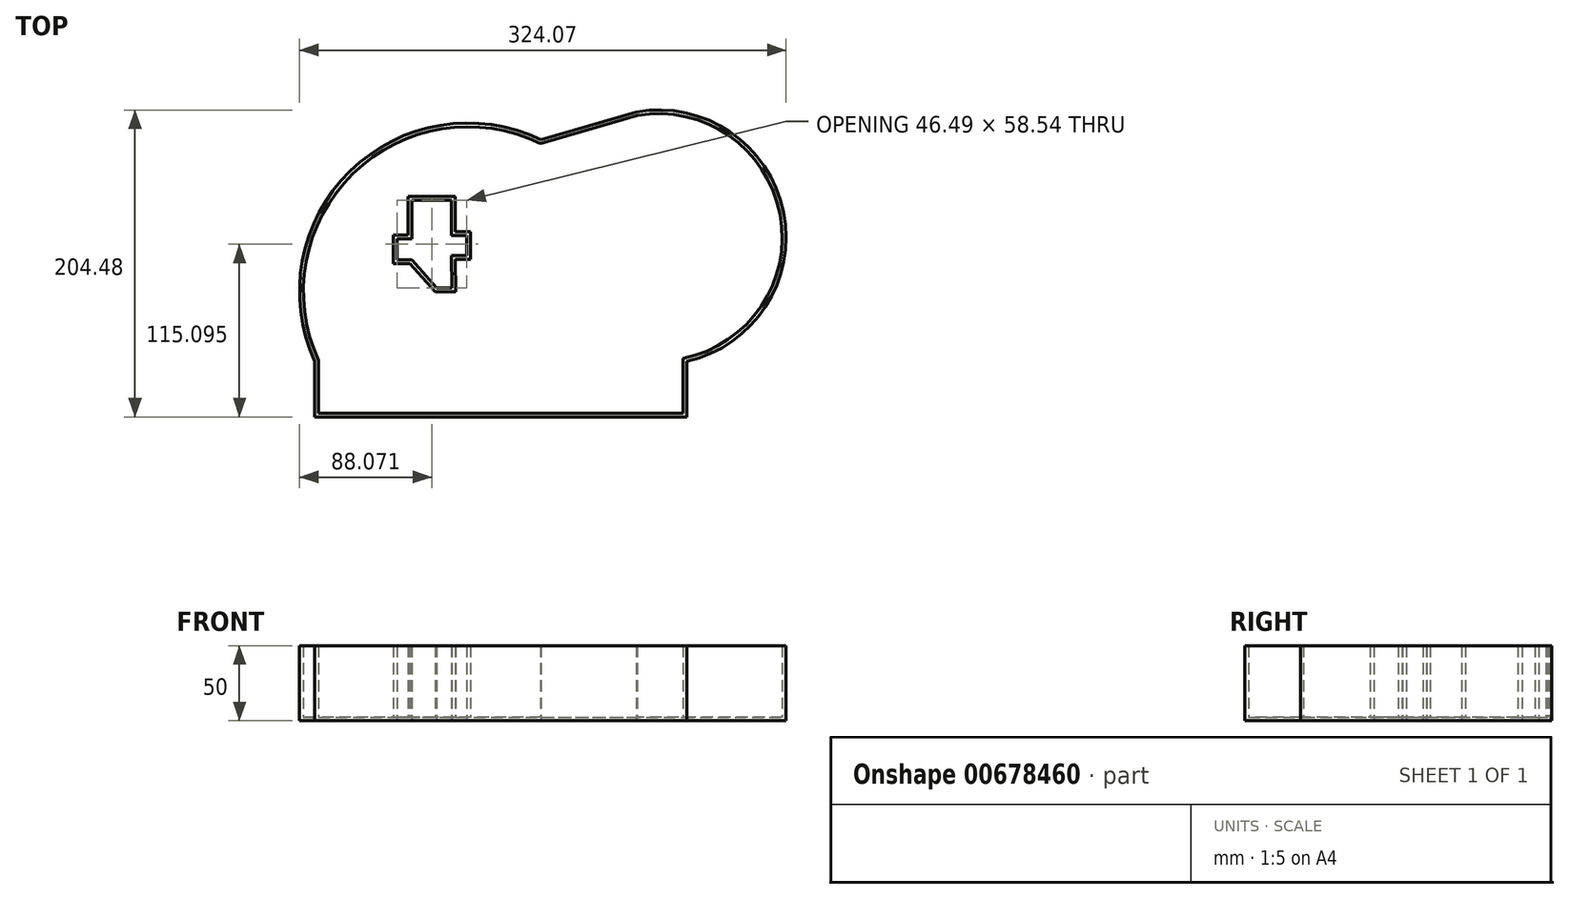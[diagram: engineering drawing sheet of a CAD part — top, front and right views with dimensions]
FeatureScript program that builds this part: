
annotation { "Feature Type Name" : "Feature", "Feature Type Description" : "" }
export const myFeature = defineFeature(function(context is Context, id is Id, definition is map)
    precondition{}
    {
        {
            var Q0;
            Q0=qCreatedBy(makeId("Top.planeOp"),FACE);
            var sketch = newSketch(context, id + "F0", { "sketchPlane" : qUnion([Q0])});
            skLineSegment(sketch, "E0", {"start": v(-101.67, -66.95) * mm, "end": v(-101.67, -103.92) * mm});
            skLineSegment(sketch, "E1", {"start": v(-101.67, -103.92) * mm, "end": v(146.19, -103.92) * mm});
            skLineSegment(sketch, "E2", {"start": v(146.19, -103.92) * mm, "end": v(146.19, -66.95) * mm});
            skArc(sketch, "E3", {"start": v(49.06, 80.77) * mm, "mid": v(-78.15, 59.81) * mm, "end": v(-101.67, -66.95) * mm});
            skLineSegment(sketch, "E4", {"start": v(49.06, 80.77) * mm, "end": v(112.57, 99.25) * mm});
            skArc(sketch, "E5", {"start": v(146.19, -66.95) * mm, "mid": v(210.57, 32.57) * mm, "end": v(112.57, 99.25) * mm});
            skLineSegment(sketch, "E6", {"start": v(-37, 0.67) * mm, "end": v(-47, 0.67) * mm});
            skLineSegment(sketch, "E7", {"start": v(-47, 0.67) * mm, "end": v(-47, 14.81) * mm});
            skLineSegment(sketch, "E8", {"start": v(-47, 14.81) * mm, "end": v(-37, 14.81) * mm});
            skLineSegment(sketch, "E9", {"start": v(-37, 14.81) * mm, "end": v(-37, 40.45) * mm});
            skLineSegment(sketch, "E10", {"start": v(-37, 40.45) * mm, "end": v(-10.77, 40.45) * mm});
            skLineSegment(sketch, "E11", {"start": v(-10.77, 40.45) * mm, "end": v(-10.7, 16.93) * mm});
            skLineSegment(sketch, "E12", {"start": v(-10.7, 16.93) * mm, "end": v(-0.54, 16.95) * mm});
            skLineSegment(sketch, "E13", {"start": v(-0.54, 16.95) * mm, "end": v(-0.5, 3.68) * mm});
            skLineSegment(sketch, "E14", {"start": v(-0.5, 3.68) * mm, "end": v(-10.5, 3.65) * mm});
            skLineSegment(sketch, "E15", {"start": v(-10.5, 3.65) * mm, "end": v(-10.4, -18.04) * mm});
            skLineSegment(sketch, "E16", {"start": v(-10.4, -18.04) * mm, "end": v(-20.4, -18.1) * mm});
            skLineSegment(sketch, "E17", {"start": v(-20.4, -18.1) * mm, "end": v(-37, 0.67) * mm});
            skSolve(sketch);
        }
        {
            var Q0;
            Q0=makeQuery(id+"F0.imprint","IMPRINT",FACE,{"disambiguationData":[TD([[makeQuery(id+"F0.imprint","IMPRINT",EDGE,{"derivedFrom":sQuery(id+"F0.wireOp",EDGE,"E0")}),1.0]])]});
            extrude(context, id + "F1", {"entities" : qUnion([Q0]), "depth" : 50 * mm, "offsetDistance" : 25 * mm});
        }
        {
            var Q0;
            Q0=makeQuery(id+"F1.opExtrude","CAP_FACE",FACE,{"disambiguationData":[OSD([sQuery(id+"F0.wireOp",EDGE,"E0"),sQuery(id+"F0.wireOp",EDGE,"E1"),sQuery(id+"F0.wireOp",EDGE,"E2"),sQuery(id+"F0.wireOp",EDGE,"E3"),sQuery(id+"F0.wireOp",EDGE,"E4"),sQuery(id+"F0.wireOp",EDGE,"E5"),sQuery(id+"F0.wireOp",EDGE,"E6"),sQuery(id+"F0.wireOp",EDGE,"E7"),sQuery(id+"F0.wireOp",EDGE,"E8"),sQuery(id+"F0.wireOp",EDGE,"E9"),sQuery(id+"F0.wireOp",EDGE,"E10"),sQuery(id+"F0.wireOp",EDGE,"E11"),sQuery(id+"F0.wireOp",EDGE,"E12"),sQuery(id+"F0.wireOp",EDGE,"E13"),sQuery(id+"F0.wireOp",EDGE,"E14"),sQuery(id+"F0.wireOp",EDGE,"E15"),sQuery(id+"F0.wireOp",EDGE,"E16"),sQuery(id+"F0.wireOp",EDGE,"E17")])],"isStart":false});
            shell(context, id + "F2", {"entities" : qUnion([Q0]), "thickness" : 2.5 * mm});
        }
    });
